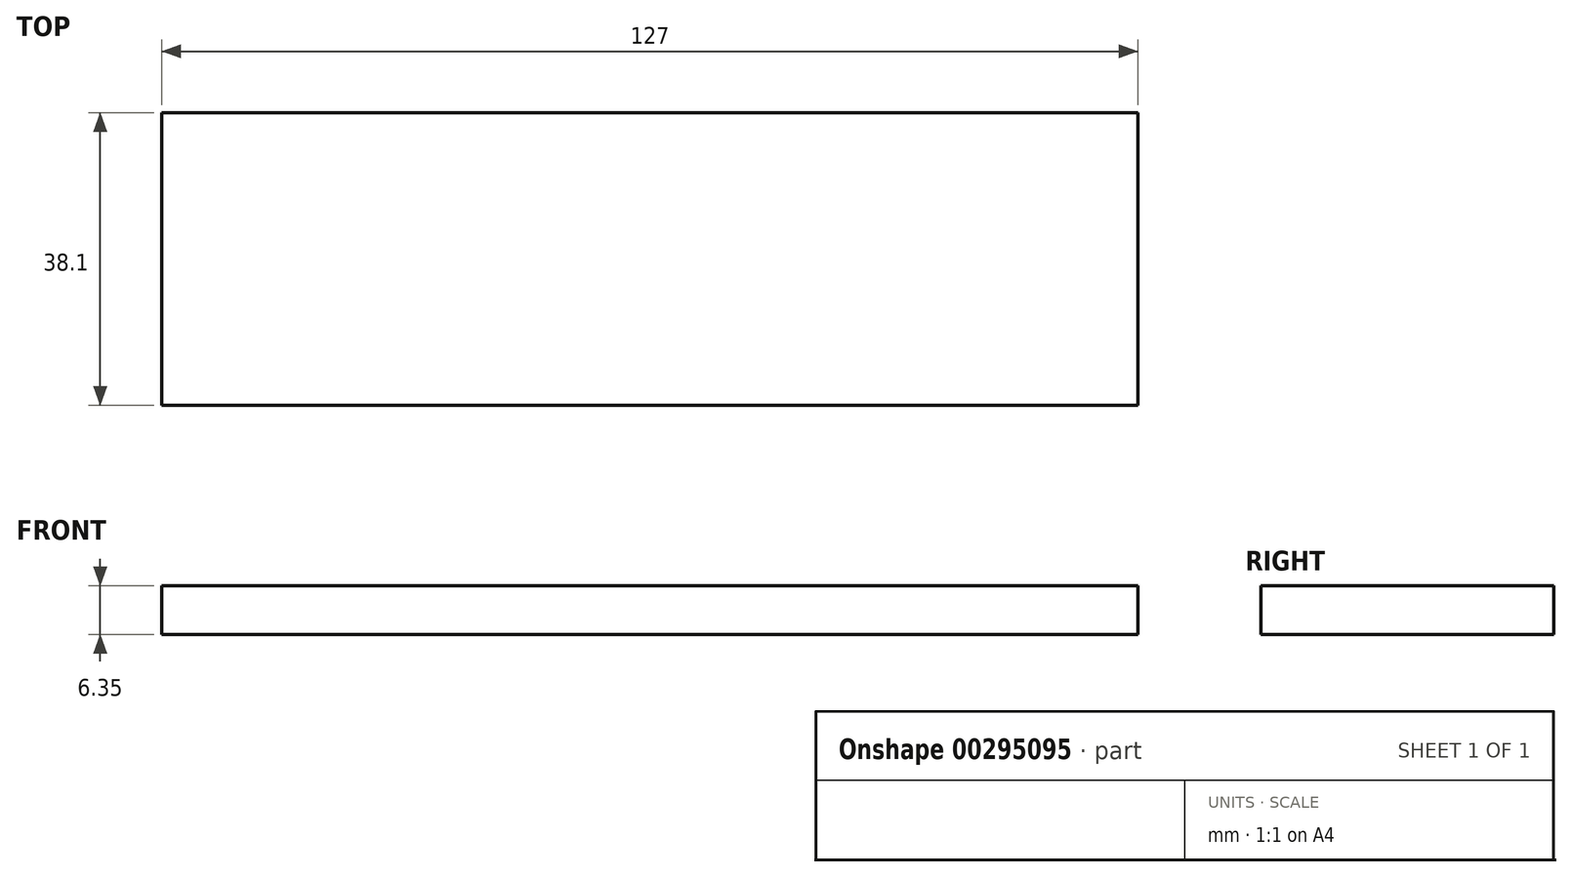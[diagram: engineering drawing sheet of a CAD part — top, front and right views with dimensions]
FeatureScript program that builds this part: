
annotation { "Feature Type Name" : "Feature", "Feature Type Description" : "" }
export const myFeature = defineFeature(function(context is Context, id is Id, definition is map)
    precondition{}
    {
        {
            var Q0;
            Q0=qCreatedBy(makeId("Top.planeOp"),FACE);
            var sketch = newSketch(context, id + "F0", { "sketchPlane" : qUnion([Q0])});
            skLineSegment(sketch, "E0.bottom", {"start": v(-31.78, 0.39) * mm, "end": v(95.22, 0.39) * mm});
            skLineSegment(sketch, "E0.top", {"start": v(-31.78, -37.71) * mm, "end": v(95.22, -37.71) * mm});
            skLineSegment(sketch, "E0.left", {"start": v(-31.78, 0.39) * mm, "end": v(-31.78, -37.71) * mm});
            skLineSegment(sketch, "E0.right", {"start": v(95.22, 0.39) * mm, "end": v(95.22, -37.71) * mm});
            skSolve(sketch);
        }
        {
            var Q0;
            Q0 = qSketchRegion(id + "F0", true);
            extrude(context, id + "F1", {"entities" : qUnion([Q0]), "depth" : 6.35 * mm});
        }
    });
